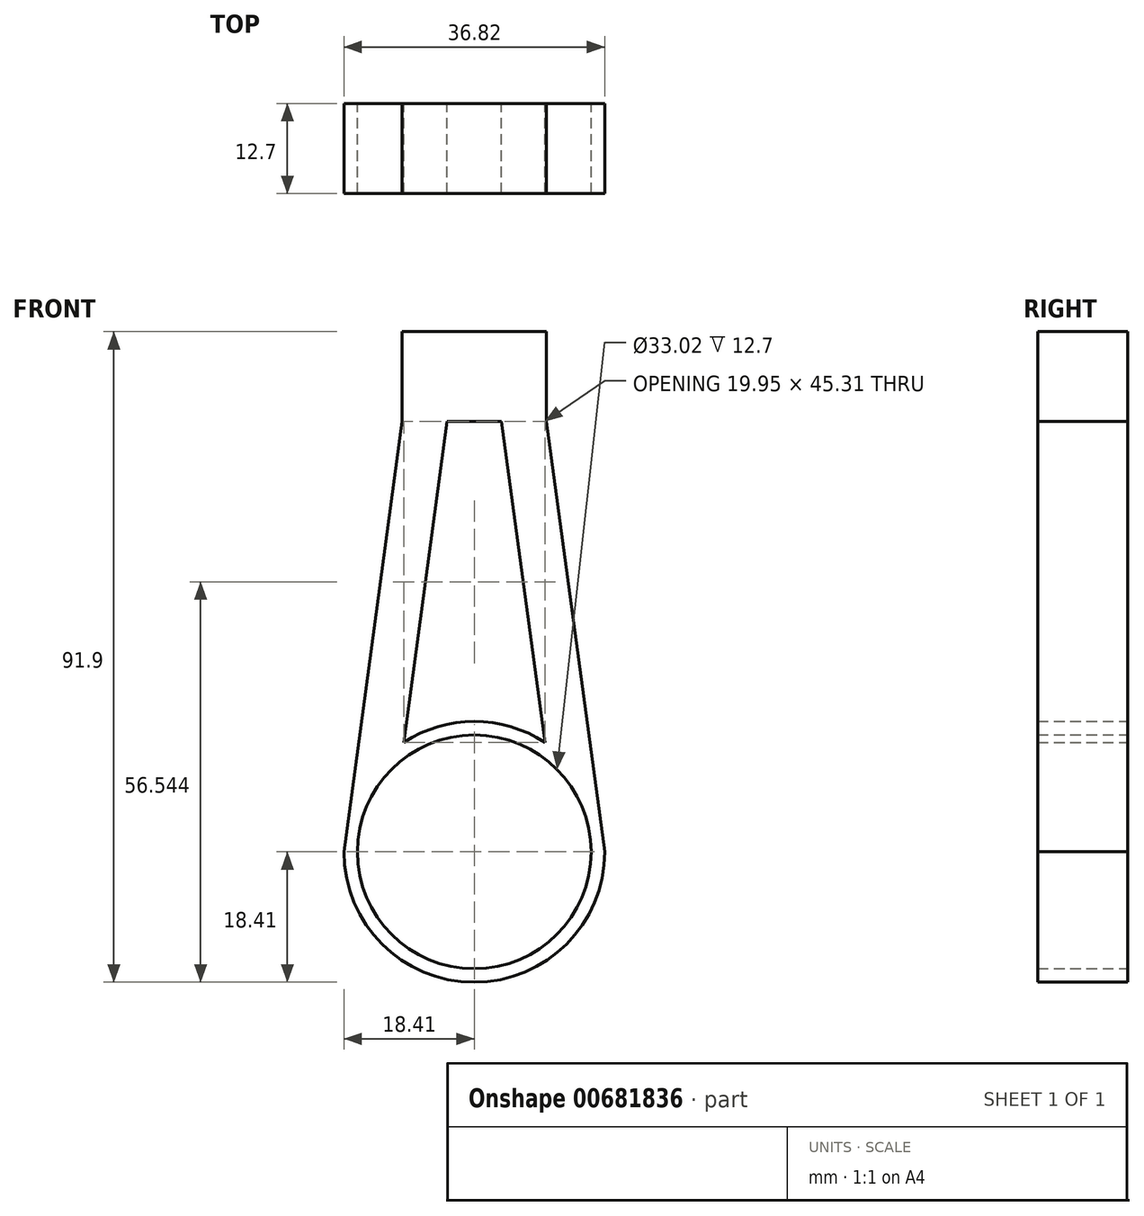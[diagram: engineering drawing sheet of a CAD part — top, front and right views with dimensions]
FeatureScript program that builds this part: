
annotation { "Feature Type Name" : "Feature", "Feature Type Description" : "" }
export const myFeature = defineFeature(function(context is Context, id is Id, definition is map)
    precondition{}
    {
        {
            var Q0;
            Q0=qCreatedBy(makeId("Front.planeOp"),FACE);
            var sketch = newSketch(context, id + "F0", { "sketchPlane" : qUnion([Q0])});
            skCircle(sketch, "E0", {"center": v(0, 0) * mm, "radius": 18.41 * mm});
            skCircle(sketch, "E1", {"center": v(0, 0) * mm, "radius": 16.51 * mm});
            skLineSegment(sketch, "E2", {"start": v(-18.41, 0) * mm, "end": v(-10.2, 60.79) * mm});
            skLineSegment(sketch, "E3", {"start": v(-10.2, 60.79) * mm, "end": v(-3.86, 60.79) * mm});
            skLineSegment(sketch, "E4", {"start": v(-3.86, 60.79) * mm, "end": v(-9.97, 15.48) * mm});
            skLineSegment(sketch, "E5", {"start": v(18.41, 0) * mm, "end": v(10.2, 60.79) * mm});
            skLineSegment(sketch, "E6", {"start": v(10.2, 60.79) * mm, "end": v(3.86, 60.79) * mm});
            skLineSegment(sketch, "E7", {"start": v(3.86, 60.79) * mm, "end": v(9.97, 15.48) * mm});
            skLineSegment(sketch, "E8", {"start": v(-3.86, 60.79) * mm, "end": v(0, 60.79) * mm});
            skLineSegment(sketch, "E9", {"start": v(0, 60.79) * mm, "end": v(3.86, 60.79) * mm});
            skLineSegment(sketch, "E10.top", {"start": v(-10.2, 73.49) * mm, "end": v(10.2, 73.49) * mm});
            skLineSegment(sketch, "E10.left", {"start": v(-10.2, 60.79) * mm, "end": v(-10.2, 73.49) * mm});
            skLineSegment(sketch, "E11", {"start": v(10.2, 73.49) * mm, "end": v(10.2, 60.79) * mm});
            skSolve(sketch);
        }
        {
            var Q0;
            Q0=makeQuery(id+"F0.imprint","IMPRINT",FACE,{"disambiguationData":[TD([[makeQuery(id+"F0.imprint","IMPRINT",EDGE,{"derivedFrom":sQuery(id+"F0.wireOp",EDGE,"E1")}),-1.0]])]});
            var Q1;
            {var subQ0=sQuery(id+"F0.wireOp",EDGE,"64n1DHZf-It2R-d08L-StdR-EtkmsXoDmst6");Q1=makeQuery(id+"F0.imprint","IMPRINT",FACE,{"disambiguationData":[TD([[makeQuery(id+"F0.imprint","IMPRINT",EDGE,{"derivedFrom":subQ0}),-1.0]])]});}
            var Q2;
            {var subQ0=sQuery(id+"F0.wireOp",EDGE,"tG5ZF7yh-CXO2-jMXo-LqFC-U6fXHawUkKIL");Q2=makeQuery(id+"F0.imprint","IMPRINT",FACE,{"disambiguationData":[TD([[makeQuery(id+"F0.imprint","IMPRINT",EDGE,{"derivedFrom":subQ0}),1.0]])]});}
            var Q3;
            {var subQ4=sQuery(id+"F0.wireOp",EDGE,"E3");Q3=makeQuery(id+"F0.imprint","IMPRINT",FACE,{"disambiguationData":[TD([[makeQuery(id+"F0.imprint","IMPRINT",EDGE,{"derivedFrom":subQ4}),-1.0]])]});}
            var Q4;
            {var subQ4=sQuery(id+"F0.wireOp",EDGE,"E6");Q4=makeQuery(id+"F0.imprint","IMPRINT",FACE,{"disambiguationData":[TD([[makeQuery(id+"F0.imprint","IMPRINT",EDGE,{"derivedFrom":subQ4}),1.0]])]});}
            var Q5;
            {var subQ0=sQuery(id+"F0.wireOp",EDGE,"E5");var subQ1=sQuery(id+"F0.wireOp",EDGE,"E0");var subQ2=makeQuery(id+"F0.imprint","INTERSECT",VERTEX,{"disambiguationData":[OD(0.0)],"derivedFrom":[subQ1,subQ0]});Q5=makeQuery(id+"F0.imprint","IMPRINT",FACE,{"disambiguationData":[TD([[makeQuery(id+"F0.imprint","IMPRINT",EDGE,{"disambiguationData":[TD([[subQ2,-1.0]])],"derivedFrom":subQ1}),1.0]])]});}
            var Q6;
            {var subQ0=sQuery(id+"F0.wireOp",EDGE,"E2");var subQ1=sQuery(id+"F0.wireOp",EDGE,"E0");var subQ2=makeQuery(id+"F0.imprint","INTERSECT",VERTEX,{"disambiguationData":[OD(0.0)],"derivedFrom":[subQ1,subQ0]});Q6=makeQuery(id+"F0.imprint","IMPRINT",FACE,{"disambiguationData":[TD([[makeQuery(id+"F0.imprint","IMPRINT",EDGE,{"disambiguationData":[TD([[subQ2,1.0]])],"derivedFrom":subQ1}),1.0]])]});}
            var Q7;
            {var subQ0=sQuery(id+"F0.wireOp",EDGE,"E7");Q7=makeQuery(id+"F0.imprint","IMPRINT",FACE,{"disambiguationData":[TD([[makeQuery(id+"F0.imprint","IMPRINT",EDGE,{"derivedFrom":subQ0}),1.0]])]});}
            var Q8;
            Q8=makeQuery(id+"F0.imprint","IMPRINT",FACE,{"disambiguationData":[TD([[makeQuery(id+"F0.imprint","IMPRINT",EDGE,{"derivedFrom":sQuery(id+"F0.wireOp",EDGE,"E10.top")}),-1.0]])]});
            var Q9;
            {var subQ0=sQuery(id+"F0.wireOp",EDGE,"E4");Q9=makeQuery(id+"F0.imprint","IMPRINT",FACE,{"disambiguationData":[TD([[makeQuery(id+"F0.imprint","IMPRINT",EDGE,{"derivedFrom":subQ0}),-1.0]])]});}
            extrude(context, id + "F1", {"entities" : qUnion([Q0, Q1, Q2, Q3, Q4, Q5, Q6, Q7, Q8, Q9]), "depth" : 12.7 * mm, "offsetDistance" : 25.4 * mm});
        }
    });
